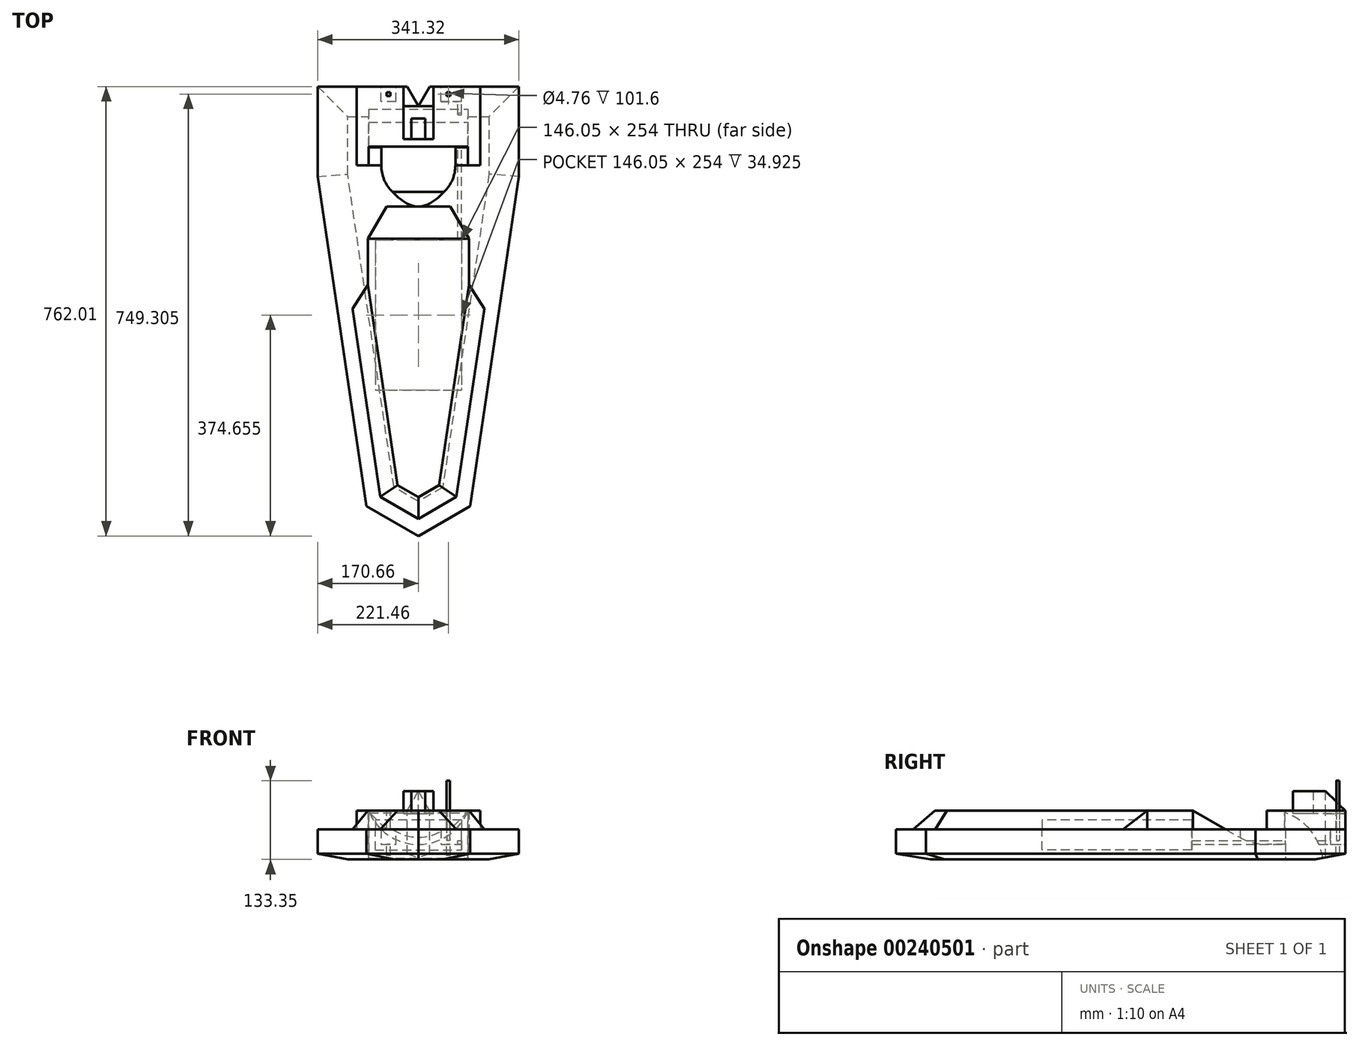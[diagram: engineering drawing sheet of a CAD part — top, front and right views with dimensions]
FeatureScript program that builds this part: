
annotation { "Feature Type Name" : "Feature", "Feature Type Description" : "" }
export const myFeature = defineFeature(function(context is Context, id is Id, definition is map)
    precondition{}
    {
        {
            var Q0;
            Q0=qCreatedBy(makeId("Top.planeOp"),FACE);
            cPlane(context, id + "F0", {"entities" : qUnion([Q0]), "cplaneType" : CPlaneType.OFFSET, "offset" : 65.1 * mm, "oppositeDirection" : true, "width" : 152.4 * mm, "height" : 152.4 * mm});
        }
        {
            var Q0;
            Q0=qCreatedBy(id+"F0.planeOp",FACE);
            var sketch = newSketch(context, id + "F1", { "sketchPlane" : qUnion([Q0])});
            skLineSegment(sketch, "E0", {"start": v(-170.66, -34.93) * mm, "end": v(-87.99, -593.73) * mm});
            skLineSegment(sketch, "E1", {"start": v(-170.66, 117.47) * mm, "end": v(0, 117.48) * mm});
            skLineSegment(sketch, "E2", {"start": v(0, -644.53) * mm, "end": v(-87.99, -593.73) * mm});
            skLineSegment(sketch, "E3", {"start": v(-170.66, -34.93) * mm, "end": v(-170.66, 117.47) * mm});
            skLineSegment(sketch, "E4", {"start": v(-73.03, -142.88) * mm, "end": v(-73.03, -396.88) * mm});
            skLineSegment(sketch, "E5", {"start": v(-73.03, -396.88) * mm, "end": v(0, -396.88) * mm});
            skLineSegment(sketch, "E6", {"start": v(-73.03, -142.88) * mm, "end": v(0, -142.88) * mm});
            skLineSegment(sketch, "E7", {"start": v(0, 117.48) * mm, "end": v(0, -644.53) * mm, "construction": true});
            skLineSegment(sketch, "E8", {"start": v(0, 0) * mm, "end": v(-88.9, 0) * mm, "construction": true});
            skLineSegment(sketch, "E9.MirrorCS", {"start": v(170.66, 117.48) * mm, "end": v(0, 117.48) * mm});
            skLineSegment(sketch, "E10.MirrorCS", {"start": v(170.66, -34.93) * mm, "end": v(170.66, 117.47) * mm});
            skLineSegment(sketch, "E11.MirrorCS", {"start": v(170.66, -34.92) * mm, "end": v(87.99, -593.73) * mm});
            skLineSegment(sketch, "E12.MirrorCS", {"start": v(0, -644.53) * mm, "end": v(87.99, -593.73) * mm});
            skLineSegment(sketch, "E13.MirrorCS", {"start": v(73.03, -396.88) * mm, "end": v(0, -396.88) * mm});
            skLineSegment(sketch, "E14.MirrorCS", {"start": v(73.03, -142.87) * mm, "end": v(73.03, -396.88) * mm});
            skLineSegment(sketch, "E15.MirrorCS", {"start": v(73.03, -142.88) * mm, "end": v(0, -142.88) * mm});
            skLineSegment(sketch, "E16.MirrorCS", {"start": v(0, 0) * mm, "end": v(88.9, 0) * mm, "construction": true});
            skSolve(sketch);
        }
        {
            var Q0;
            Q0=makeQuery(id+"F1.imprint","IMPRINT",FACE,{"disambiguationData":[TD([[makeQuery(id+"F1.imprint","IMPRINT",EDGE,{"derivedFrom":sQuery(id+"F1.wireOp",EDGE,"E4")}),1.0]])]});
            var Q1;
            Q1=makeQuery(id+"F1.imprint","IMPRINT",FACE,{"disambiguationData":[TD([[makeQuery(id+"F1.imprint","IMPRINT",EDGE,{"derivedFrom":sQuery(id+"F1.wireOp",EDGE,"E0")}),1.0]])]});
            extrude(context, id + "F2", {"entities" : qUnion([Q0, Q1]), "oppositeDirection" : true, "depth" : 50.8 * mm});
        }
        {
            var Q0;
            Q0=makeQuery(id+"F1.imprint","IMPRINT",FACE,{"disambiguationData":[TD([[makeQuery(id+"F1.imprint","IMPRINT",EDGE,{"derivedFrom":sQuery(id+"F1.wireOp",EDGE,"E4")}),1.0]])]});
            extrude(context, id + "F3", {"entities" : qUnion([Q0]), "operationType" : NewBodyOperationType.REMOVE, "oppositeDirection" : true, "depth" : 34.92 * mm});
        }
        {
            var Q0;
            Q0=makeQuery(id+"F2.opExtrude","CAP_EDGE",EDGE,{"disambiguationData":[OSD([sQuery(id+"F1.wireOp",EDGE,"E1"),sQuery(id+"F1.wireOp",EDGE,"E9.MirrorCS")])],"isStart":false});
            var Q1;
            Q1=makeQuery(id+"F2.opExtrude","CAP_EDGE",EDGE,{"disambiguationData":[OSD([sQuery(id+"F1.wireOp",EDGE,"E3")])],"isStart":false});
            var Q2;
            Q2=makeQuery(id+"F2.opExtrude","CAP_EDGE",EDGE,{"disambiguationData":[OSD([sQuery(id+"F1.wireOp",EDGE,"E0")])],"isStart":false});
            var Q3;
            Q3=makeQuery(id+"F2.opExtrude","CAP_EDGE",EDGE,{"disambiguationData":[OSD([sQuery(id+"F1.wireOp",EDGE,"E2")])],"isStart":false});
            var Q4;
            Q4=makeQuery(id+"F2.opExtrude","CAP_EDGE",EDGE,{"disambiguationData":[OSD([sQuery(id+"F1.wireOp",EDGE,"E12.MirrorCS")])],"isStart":false});
            var Q5;
            Q5=makeQuery(id+"F2.opExtrude","CAP_EDGE",EDGE,{"disambiguationData":[OSD([sQuery(id+"F1.wireOp",EDGE,"E11.MirrorCS")])],"isStart":false});
            var Q6;
            Q6=makeQuery(id+"F2.opExtrude","CAP_EDGE",EDGE,{"disambiguationData":[OSD([sQuery(id+"F1.wireOp",EDGE,"E10.MirrorCS")])],"isStart":false});
            chamfer(context, id + "F4", {"entities" : qUnion([Q0, Q1, Q2, Q3, Q4, Q5, Q6]), "chamferType" : ChamferType.TWO_OFFSETS, "width1" : 50.8 * mm, "oppositeDirection" : true, "width2" : 9.52 * mm, "tangentPropagation" : true});
        }
        {
            var Q0;
            Q0=qCreatedBy(makeId("Right.planeOp"),FACE);
            var sketch = newSketch(context, id + "F5", { "sketchPlane" : qUnion([Q0])});
            skLineSegment(sketch, "E17", {"start": v(15.88, -65.09) * mm, "end": v(15.88, -115.89) * mm});
            skArc(sketch, "E18", {"start": v(57.15, -65.09) * mm, "mid": v(72.04, -88.84) * mm, "end": v(79.37, -115.89) * mm});
            skLineSegment(sketch, "E19", {"start": v(15.88, -65.09) * mm, "end": v(57.15, -65.09) * mm});
            skLineSegment(sketch, "E20", {"start": v(15.88, -115.89) * mm, "end": v(79.37, -115.89) * mm});
            skSolve(sketch);
        }
        {
            var Q0;
            Q0 = qSketchRegion(id + "F5", true);
            extrude(context, id + "F6", {"entities" : qUnion([Q0]), "operationType" : NewBodyOperationType.REMOVE, "oppositeDirection" : true, "depth" : 168.27 * mm, "symmetric" : true});
        }
        {
            var Q0;
            Q0=qCreatedBy(makeId("Top.planeOp"),FACE);
            cPlane(context, id + "F7", {"entities" : qUnion([Q0]), "cplaneType" : CPlaneType.OFFSET, "offset" : 65.1 * mm, "oppositeDirection" : true, "width" : 152.4 * mm, "height" : 152.4 * mm});
        }
        {
            var Q0;
            Q0=qCreatedBy(id+"F7.planeOp",FACE);
            var sketch = newSketch(context, id + "F8", { "sketchPlane" : qUnion([Q0])});
            skLineSegment(sketch, "E21.0", {"start": v(-170.66, -34.93) * mm, "end": v(-87.99, -593.73) * mm, "construction": true});
            skLineSegment(sketch, "E21.1", {"start": v(0, -644.53) * mm, "end": v(-87.99, -593.73) * mm, "construction": true});
            skLineSegment(sketch, "E21.2", {"start": v(0, -644.53) * mm, "end": v(87.99, -593.73) * mm, "construction": true});
            skLineSegment(sketch, "E21.3", {"start": v(170.66, -34.92) * mm, "end": v(87.99, -593.73) * mm, "construction": true});
            skLineSegment(sketch, "E22", {"start": v(-111.77, -259.4) * mm, "end": v(-64.66, -577.87) * mm});
            skLineSegment(sketch, "E23", {"start": v(-64.66, -577.87) * mm, "end": v(0, -615.2) * mm});
            skLineSegment(sketch, "E24", {"start": v(0, -615.2) * mm, "end": v(64.66, -577.87) * mm});
            skLineSegment(sketch, "E25", {"start": v(64.66, -577.87) * mm, "end": v(111.77, -259.4) * mm});
            skLineSegment(sketch, "E26.0", {"start": v(-73.03, -396.88) * mm, "end": v(73.03, -396.87) * mm});
            skLineSegment(sketch, "E26.1", {"start": v(73.03, -142.87) * mm, "end": v(-73.03, -142.88) * mm});
            skLineSegment(sketch, "E26.2", {"start": v(73.03, -142.87) * mm, "end": v(73.03, -396.87) * mm});
            skLineSegment(sketch, "E26.3", {"start": v(-73.03, -142.88) * mm, "end": v(-73.03, -396.88) * mm});
            skLineSegment(sketch, "E27", {"start": v(-53.97, -85.73) * mm, "end": v(53.98, -85.72) * mm});
            skLineSegment(sketch, "E28", {"start": v(0, -615.2) * mm, "end": v(0, -52.66) * mm, "construction": true});
            skLineSegment(sketch, "E29", {"start": v(85.73, -140.72) * mm, "end": v(85.73, -218.5) * mm});
            skLineSegment(sketch, "E30", {"start": v(-85.72, -140.72) * mm, "end": v(-85.72, -218.5) * mm});
            skLineSegment(sketch, "E31", {"start": v(85.73, -218.5) * mm, "end": v(111.77, -259.4) * mm});
            skLineSegment(sketch, "E32", {"start": v(-85.72, -218.5) * mm, "end": v(-111.77, -259.4) * mm});
            skLineSegment(sketch, "E33", {"start": v(-111.77, -259.4) * mm, "end": v(111.77, -259.4) * mm, "construction": true});
            skLineSegment(sketch, "E34", {"start": v(-85.72, -140.72) * mm, "end": v(-53.97, -85.72) * mm});
            skLineSegment(sketch, "E35", {"start": v(85.73, -140.72) * mm, "end": v(53.98, -85.72) * mm});
            skLineSegment(sketch, "E36", {"start": v(-85.72, -140.72) * mm, "end": v(85.73, -140.72) * mm, "construction": true});
            skSolve(sketch);
        }
        {
            var Q0;
            Q0 = qSketchRegion(id + "F8", true);
            var Q1;
            Q1=makeQuery(id+"F8.imprint","IMPRINT",FACE,{"disambiguationData":[TD([[makeQuery(id+"F8.imprint","IMPRINT",EDGE,{"derivedFrom":sQuery(id+"F8.wireOp",EDGE,"E26.0")}),1.0]])]});
            extrude(context, id + "F9", {"entities" : qUnion([Q0, Q1]), "depth" : 31.75 * mm});
        }
        {
            var Q0;
            Q0=makeQuery(id+"F9.opExtrude","CAP_EDGE",EDGE,{"disambiguationData":[OSD([sQuery(id+"F8.wireOp",EDGE,"E25")])],"isStart":false});
            var Q1;
            Q1=makeQuery(id+"F9.opExtrude","CAP_EDGE",EDGE,{"disambiguationData":[OSD([sQuery(id+"F8.wireOp",EDGE,"E24")])],"isStart":false});
            var Q2;
            Q2=makeQuery(id+"F9.opExtrude","CAP_EDGE",EDGE,{"disambiguationData":[OSD([sQuery(id+"F8.wireOp",EDGE,"E23")])],"isStart":false});
            var Q3;
            Q3=makeQuery(id+"F9.opExtrude","CAP_EDGE",EDGE,{"disambiguationData":[OSD([sQuery(id+"F8.wireOp",EDGE,"E22")])],"isStart":false});
            chamfer(context, id + "F10", {"entities" : qUnion([Q0, Q1, Q2, Q3]), "width" : 31.75 * mm, "tangentPropagation" : true});
        }
        {
            var Q0;
            Q0=makeQuery(id+"F9.opExtrude","CAP_EDGE",EDGE,{"disambiguationData":[OSD([sQuery(id+"F8.wireOp",EDGE,"E27")])],"isStart":false});
            chamfer(context, id + "F11", {"entities" : qUnion([Q0]), "chamferType" : ChamferType.OFFSET_ANGLE, "width" : 31.75 * mm, "oppositeDirection" : false, "angle" : 60 * degree, "tangentPropagation" : true});
        }
        {
            var Q0;
            Q0=makeQuery(id+"F8.imprint","IMPRINT",FACE,{"disambiguationData":[TD([[makeQuery(id+"F8.imprint","IMPRINT",EDGE,{"derivedFrom":sQuery(id+"F8.wireOp",EDGE,"E26.0")}),1.0]])]});
            extrude(context, id + "F12", {"entities" : qUnion([Q0]), "operationType" : NewBodyOperationType.REMOVE, "depth" : 15.88 * mm});
        }
        {
            var Q0;
            Q0=qCreatedBy(id+"F7.planeOp",FACE);
            var sketch = newSketch(context, id + "F13", { "sketchPlane" : qUnion([Q0])});
            skLineSegment(sketch, "E37.bottom", {"start": v(-104.78, 117.48) * mm, "end": v(104.78, 117.48) * mm});
            skLineSegment(sketch, "E37.top", {"start": v(-104.77, -15.88) * mm, "end": v(104.78, -15.88) * mm});
            skLineSegment(sketch, "E37.left", {"start": v(-104.78, 117.48) * mm, "end": v(-104.77, -15.88) * mm});
            skLineSegment(sketch, "E37.right", {"start": v(104.78, 117.48) * mm, "end": v(104.78, -15.87) * mm});
            skLineSegment(sketch, "E38", {"start": v(0, 117.48) * mm, "end": v(0, -15.88) * mm, "construction": true});
            skSolve(sketch);
        }
        {
            var Q0;
            Q0 = qSketchRegion(id + "F13", true);
            extrude(context, id + "F14", {"entities" : qUnion([Q0]), "depth" : 31.75 * mm});
        }
        {
            var Q0;
            Q0=makeQuery(id+"F14.opExtrude","SWEPT_FACE",FACE,{"disambiguationData":[OSD([sQuery(id+"F13.wireOp",EDGE,"E37.top")])]});
            cPlane(context, id + "F15", {"entities" : qUnion([Q0]), "cplaneType" : CPlaneType.OFFSET, "offset" : 15.88 * mm, "oppositeDirection" : true, "width" : 152.4 * mm, "height" : 152.4 * mm});
        }
        {
            var Q0;
            Q0=qCreatedBy(id+"F15.planeOp",FACE);
            var sketch = newSketch(context, id + "F16", { "sketchPlane" : qUnion([Q0])});
            skCircle(sketch, "E39", {"center": v(0, 0) * mm, "radius": 90.49 * mm});
            skSolve(sketch);
        }
        {
            var Q0;
            Q0=qCreatedBy(makeId("Right.planeOp"),FACE);
            var sketch = newSketch(context, id + "F17", { "sketchPlane" : qUnion([Q0])});
            skArc(sketch, "E40.0", {"start": v(57.15, -65.09) * mm, "mid": v(72.04, -88.84) * mm, "end": v(79.37, -115.89) * mm, "construction": true});
            skArc(sketch, "E41", {"start": v(57.15, -65.09) * mm, "mid": v(37.8, -47.87) * mm, "end": v(14.5, -36.51) * mm});
            skLineSegment(sketch, "E42", {"start": v(14.5, -36.51) * mm, "end": v(14.5, -33.34) * mm, "construction": true});
            skLineSegment(sketch, "E43", {"start": v(79.37, -115.89) * mm, "end": v(-15.23, -115.89) * mm, "construction": true});
            skLineSegment(sketch, "E44", {"start": v(57.15, -65.09) * mm, "end": v(-15.23, -65.09) * mm, "construction": true});
            skLineSegment(sketch, "E45", {"start": v(14.5, -33.34) * mm, "end": v(-34.43, -33.34) * mm, "construction": true});
            skLineSegment(sketch, "E46", {"start": v(14.5, -36.51) * mm, "end": v(14.5, -65.09) * mm});
            skLineSegment(sketch, "E47", {"start": v(14.5, -65.09) * mm, "end": v(57.15, -65.09) * mm});
            skSolve(sketch);
        }
        {
            var Q0;
            Q0=makeQuery(id+"F17.imprint","IMPRINT",FACE,{"disambiguationData":[TD([[makeQuery(id+"F17.imprint","IMPRINT",EDGE,{"derivedFrom":sQuery(id+"F17.wireOp",EDGE,"E41")}),1.0]])]});
            extrude(context, id + "F18", {"entities" : qUnion([Q0]), "operationType" : NewBodyOperationType.REMOVE, "oppositeDirection" : true, "depth" : 168.27 * mm, "symmetric" : true});
        }
        {
            var Q0;
            Q0 = qSketchRegion(id + "F16", true);
            var Q1;
            Q1=makeQuery(id+"F6.boolean.opBoolean","COPY",FACE,{"derivedFrom":makeQuery(id+"F6.opExtrude","SWEPT_FACE",FACE,{"disambiguationData":[OSD([sQuery(id+"F5.wireOp",EDGE,"E17")])]})});
            var Q2;
            Q2=makeQuery(id+"F14.opExtrude","SWEPT_FACE",FACE,{"disambiguationData":[OSD([sQuery(id+"F13.wireOp",EDGE,"E37.top")])]});
            extrude(context, id + "F19", {"entities" : qUnion([Q0]), "operationType" : NewBodyOperationType.REMOVE, "endBound" : BoundingType.UP_TO_SURFACE, "oppositeDirection" : true, "endBoundEntityFace" : qUnion([Q1]), "depth" : 30.16 * mm, "hasSecondDirection" : true, "secondDirectionBound" : BoundingType.UP_TO_SURFACE, "secondDirectionOppositeDirection" : false, "secondDirectionBoundEntityFace" : qUnion([Q2]), "secondDirectionDepth" : 25.4 * mm});
        }
        {
            var Q0;
            Q0=qCreatedBy(makeId("Right.planeOp"),FACE);
            var sketch = newSketch(context, id + "F20", { "sketchPlane" : qUnion([Q0])});
            skLineSegment(sketch, "E48", {"start": v(0, -90.49) * mm, "end": v(-85.73, -65.09) * mm, "construction": true});
            skPoint(sketch, "E49.0", {"position": v(0, 0) * mm});
            skArc(sketch, "E50", {"start": v(-15.87, -90.49) * mm, "mid": v(-39.3, -87.4) * mm, "end": v(-61.12, -78.36) * mm});
            skLineSegment(sketch, "E51", {"start": v(-15.87, 0) * mm, "end": v(-61.12, -78.36) * mm, "construction": true});
            skLineSegment(sketch, "E52", {"start": v(-61.12, -78.36) * mm, "end": v(-85.73, -65.09) * mm});
            skLineSegment(sketch, "E53", {"start": v(-85.73, -65.09) * mm, "end": v(0, -65.09) * mm});
            skLineSegment(sketch, "E54", {"start": v(0, -65.09) * mm, "end": v(0, -90.49) * mm});
            skLineSegment(sketch, "E55", {"start": v(0, 0) * mm, "end": v(-85.73, 0) * mm, "construction": true});
            skLineSegment(sketch, "E56", {"start": v(0, -90.49) * mm, "end": v(-15.87, -90.49) * mm});
            skSolve(sketch);
        }
        {
            var Q0;
            Q0 = qSketchRegion(id + "F20", true);
            var Q1;
            Q1=sQuery(id+"F20.wireOp",EDGE,"E55");
            revolve(context, id + "F21", {"operationType" : NewBodyOperationType.REMOVE, "entities" : qUnion([Q0]), "axis" : qUnion([Q1]), "revolveType" : RevolveType.FULL, "oppositeDirection" : true});
        }
        {
            var Q0;
            Q0=makeQuery(id+"F4.opChamfer","BLEND_FACE",FACE,{"disambiguationData":[OSD([sQuery(id+"F1.wireOp",EDGE,"E1"),sQuery(id+"F1.wireOp",EDGE,"E9.MirrorCS")])]});
            var Q1;
            Q1=makeQuery(id+"F6.boolean.opBoolean","INTERSECT",EDGE,{"derivedFrom":[makeQuery(id+"F4.opChamfer","BLEND_FACE",FACE,{"disambiguationData":[OSD([sQuery(id+"F1.wireOp",EDGE,"E1"),sQuery(id+"F1.wireOp",EDGE,"E9.MirrorCS")])]}),makeQuery(id+"F6.opExtrude","SWEPT_FACE",FACE,{"disambiguationData":[OSD([sQuery(id+"F5.wireOp",EDGE,"E18")])]})]});
            cPlane(context, id + "F22", {"entities" : qUnion([Q0, Q1]), "cplaneType" : CPlaneType.LINE_ANGLE, "offset" : 25.4 * mm, "angle" : 90 * degree, "width" : 152.4 * mm, "height" : 152.4 * mm});
        }
        {
            var Q0;
            Q0=makeQuery(id+"F14.opExtrude","CAP_FACE",FACE,{"disambiguationData":[OSD([sQuery(id+"F13.wireOp",EDGE,"E37.bottom"),sQuery(id+"F13.wireOp",EDGE,"E37.top"),sQuery(id+"F13.wireOp",EDGE,"E37.left"),sQuery(id+"F13.wireOp",EDGE,"E37.right")])],"isStart":false});
            var sketch = newSketch(context, id + "F23", { "sketchPlane" : qUnion([Q0])});
            skLineSegment(sketch, "E57", {"start": v(0, 117.47) * mm, "end": v(0, 15.88) * mm, "construction": true});
            skLineSegment(sketch, "E58", {"start": v(-25.4, 117.47) * mm, "end": v(-25.4, 28.58) * mm});
            skLineSegment(sketch, "E59", {"start": v(-25.4, 28.58) * mm, "end": v(25.4, 28.58) * mm});
            skLineSegment(sketch, "E60", {"start": v(25.4, 28.57) * mm, "end": v(25.4, 117.48) * mm});
            skLineSegment(sketch, "E61", {"start": v(-25.4, 117.48) * mm, "end": v(25.4, 117.48) * mm});
            skSolve(sketch);
        }
        {
            var Q0;
            Q0 = qSketchRegion(id + "F23", true);
            extrude(context, id + "F24", {"entities" : qUnion([Q0]), "operationType" : NewBodyOperationType.REMOVE, "oppositeDirection" : true, "depth" : 4.76 * mm});
        }
        {
            var Q0;
            Q0=qCreatedBy(makeId("Top.planeOp"),FACE);
            cPlane(context, id + "F25", {"entities" : qUnion([Q0]), "cplaneType" : CPlaneType.OFFSET, "offset" : 38.1 * mm, "oppositeDirection" : true, "width" : 152.4 * mm, "height" : 152.4 * mm});
        }
        {
            var Q0;
            Q0=qCreatedBy(id+"F25.planeOp",FACE);
            var sketch = newSketch(context, id + "F26", { "sketchPlane" : qUnion([Q0])});
            skLineSegment(sketch, "E62", {"start": v(0, 24.05) * mm, "end": v(0, -116.01) * mm, "construction": true});
            skPoint(sketch, "E62.startSnap0", {"position": v(0, 117.48) * mm});
            skLineSegment(sketch, "E63", {"start": v(-25.4, 117.48) * mm, "end": v(25.4, 117.48) * mm});
            skLineSegment(sketch, "E64", {"start": v(25.4, 117.48) * mm, "end": v(25.4, 28.58) * mm});
            skLineSegment(sketch, "E65", {"start": v(25.4, 28.58) * mm, "end": v(-25.4, 28.58) * mm});
            skLineSegment(sketch, "E66", {"start": v(-25.4, 28.58) * mm, "end": v(-25.4, 117.48) * mm});
            skSolve(sketch);
        }
        {
            var Q0;
            Q0 = qSketchRegion(id + "F26", true);
            extrude(context, id + "F27", {"entities" : qUnion([Q0]), "depth" : 38.1 * mm});
        }
        {
            var Q0;
            Q0=makeQuery(id+"F27.opExtrude","CAP_FACE",FACE,{"disambiguationData":[OSD([sQuery(id+"F26.wireOp",EDGE,"E63"),sQuery(id+"F26.wireOp",EDGE,"E64"),sQuery(id+"F26.wireOp",EDGE,"E65"),sQuery(id+"F26.wireOp",EDGE,"E66")])],"isStart":false});
            var sketch = newSketch(context, id + "F28", { "sketchPlane" : qUnion([Q0])});
            skLineSegment(sketch, "E67", {"start": v(0, 11.6) * mm, "end": v(0, -95.3) * mm, "construction": true});
            skPoint(sketch, "E67.startSnap0", {"position": v(0, 117.48) * mm});
            skLineSegment(sketch, "E68", {"start": v(11.9, 28.58) * mm, "end": v(11.9, 63.5) * mm});
            skLineSegment(sketch, "E69", {"start": v(11.9, 63.5) * mm, "end": v(-11.9, 63.5) * mm});
            skLineSegment(sketch, "E70", {"start": v(-11.9, 63.5) * mm, "end": v(-11.9, 28.58) * mm});
            skLineSegment(sketch, "E71", {"start": v(-11.9, 28.57) * mm, "end": v(11.9, 28.58) * mm});
            skSolve(sketch);
        }
        {
            var Q0;
            Q0 = qSketchRegion(id + "F28", true);
            extrude(context, id + "F29", {"entities" : qUnion([Q0]), "operationType" : NewBodyOperationType.REMOVE, "endBound" : BoundingType.UP_TO_NEXT, "oppositeDirection" : true, "depth" : 25.4 * mm});
        }
        {
            var Q0;
            Q0=makeQuery(id+"F27.opExtrude","CAP_EDGE",EDGE,{"disambiguationData":[OSD([sQuery(id+"F26.wireOp",EDGE,"E63")])],"isStart":false});
            chamfer(context, id + "F30", {"entities" : qUnion([Q0]), "width" : 33.34 * mm, "tangentPropagation" : true});
        }
        {
            var Q0;
            Q0=makeQuery(id+"F27.opExtrude","CAP_FACE",FACE,{"disambiguationData":[OSD([sQuery(id+"F26.wireOp",EDGE,"E63"),sQuery(id+"F26.wireOp",EDGE,"E64"),sQuery(id+"F26.wireOp",EDGE,"E65"),sQuery(id+"F26.wireOp",EDGE,"E66")])],"isStart":false});
            var sketch = newSketch(context, id + "F31", { "sketchPlane" : qUnion([Q0])});
            skLineSegment(sketch, "E72", {"start": v(0, 3.76) * mm, "end": v(0, 84.14) * mm, "construction": true});
            skLineSegment(sketch, "E73", {"start": v(0, 84.14) * mm, "end": v(19.05, 117.48) * mm});
            skLineSegment(sketch, "E74", {"start": v(0, 84.14) * mm, "end": v(-19.05, 117.48) * mm});
            skLineSegment(sketch, "E75", {"start": v(-19.05, 117.48) * mm, "end": v(19.05, 117.48) * mm});
            skSolve(sketch);
        }
        {
            var Q0;
            Q0 = qSketchRegion(id + "F31", true);
            extrude(context, id + "F32", {"entities" : qUnion([Q0]), "operationType" : NewBodyOperationType.REMOVE, "endBound" : BoundingType.THROUGH_ALL, "oppositeDirection" : true, "depth" : 25.4 * mm});
        }
        {
            var Q0;
            Q0=makeQuery(id+"F14.opExtrude","CAP_FACE",FACE,{"disambiguationData":[OSD([sQuery(id+"F13.wireOp",EDGE,"E37.bottom"),sQuery(id+"F13.wireOp",EDGE,"E37.top"),sQuery(id+"F13.wireOp",EDGE,"E37.left"),sQuery(id+"F13.wireOp",EDGE,"E37.right")])],"isStart":false});
            var sketch = newSketch(context, id + "F33", { "sketchPlane" : qUnion([Q0])});
            skLineSegment(sketch, "E76.bottom", {"start": v(-53.97, 107.95) * mm, "end": v(-47.63, 107.95) * mm});
            skLineSegment(sketch, "E76.top", {"start": v(-53.97, 101.6) * mm, "end": v(-47.63, 101.6) * mm});
            skLineSegment(sketch, "E76.left", {"start": v(-53.98, 107.95) * mm, "end": v(-53.98, 101.6) * mm});
            skLineSegment(sketch, "E76.right", {"start": v(-47.63, 107.95) * mm, "end": v(-47.63, 101.6) * mm});
            skLineSegment(sketch, "E77.bottom", {"start": v(47.63, 107.95) * mm, "end": v(53.98, 107.95) * mm});
            skLineSegment(sketch, "E77.top", {"start": v(47.63, 101.6) * mm, "end": v(53.98, 101.6) * mm});
            skLineSegment(sketch, "E77.left", {"start": v(47.63, 107.95) * mm, "end": v(47.63, 101.6) * mm});
            skLineSegment(sketch, "E77.right", {"start": v(53.98, 107.95) * mm, "end": v(53.98, 101.6) * mm});
            skLineSegment(sketch, "E78", {"start": v(-50.8, 107.95) * mm, "end": v(-50.8, 101.6) * mm, "construction": true});
            skLineSegment(sketch, "E79", {"start": v(50.8, 107.95) * mm, "end": v(50.8, 101.6) * mm, "construction": true});
            skLineSegment(sketch, "E80", {"start": v(0, 15.88) * mm, "end": v(0, 25.14) * mm, "construction": true});
            skSolve(sketch);
        }
        {
            var Q0;
            Q0 = qSketchRegion(id + "F33", true);
            extrude(context, id + "F34", {"entities" : qUnion([Q0]), "operationType" : NewBodyOperationType.REMOVE, "endBound" : BoundingType.THROUGH_ALL, "oppositeDirection" : true, "depth" : 25.4 * mm});
        }
        {
            var Q0;
            Q0=makeQuery(id+"F2.opExtrude","SWEPT_FACE",FACE,{"disambiguationData":[OSD([sQuery(id+"F1.wireOp",EDGE,"E1"),sQuery(id+"F1.wireOp",EDGE,"E9.MirrorCS")])]});
            var sketch = newSketch(context, id + "F35", { "sketchPlane" : qUnion([Q0])});
            skLineSegment(sketch, "E81", {"start": v(0, 0) * mm, "end": v(0, -106.36) * mm, "construction": true});
            skLineSegment(sketch, "E82", {"start": v(-73.02, -65.09) * mm, "end": v(-38.1, -65.09) * mm});
            skLineSegment(sketch, "E83", {"start": v(-38.1, -65.09) * mm, "end": v(-38.1, -90.49) * mm});
            skLineSegment(sketch, "E84", {"start": v(-38.1, -90.49) * mm, "end": v(-73.02, -90.49) * mm});
            skLineSegment(sketch, "E85", {"start": v(-73.03, -90.49) * mm, "end": v(-73.03, -65.09) * mm});
            skLineSegment(sketch, "E86", {"start": v(38.1, -65.09) * mm, "end": v(63.5, -65.09) * mm});
            skLineSegment(sketch, "E87", {"start": v(63.5, -65.09) * mm, "end": v(63.5, -90.49) * mm});
            skLineSegment(sketch, "E88", {"start": v(63.5, -90.49) * mm, "end": v(38.1, -90.49) * mm});
            skLineSegment(sketch, "E89", {"start": v(38.1, -90.49) * mm, "end": v(38.1, -65.09) * mm});
            skSolve(sketch);
        }
        {
            var Q0;
            Q0 = qSketchRegion(id + "F35", true);
            extrude(context, id + "F36", {"entities" : qUnion([Q0]), "operationType" : NewBodyOperationType.REMOVE, "oppositeDirection" : true, "depth" : 25.4 * mm});
        }
        {
            var Q0;
            Q0=makeQuery(id+"F36.boolean.opBoolean","COPY",FACE,{"derivedFrom":makeQuery(id+"F36.opExtrude","CAP_FACE",FACE,{"disambiguationData":[OSD([sQuery(id+"F35.wireOp",EDGE,"E82"),sQuery(id+"F35.wireOp",EDGE,"E83"),sQuery(id+"F35.wireOp",EDGE,"E84"),sQuery(id+"F35.wireOp",EDGE,"E85")])],"isStart":false})});
            var sketch = newSketch(context, id + "F37", { "sketchPlane" : qUnion([Q0])});
            skLineSegment(sketch, "E90", {"start": v(-73.03, -84.14) * mm, "end": v(-66.67, -84.14) * mm});
            skLineSegment(sketch, "E91", {"start": v(-66.67, -84.14) * mm, "end": v(-66.67, -90.49) * mm});
            skLineSegment(sketch, "E92", {"start": v(-66.67, -90.49) * mm, "end": v(-73.03, -90.49) * mm});
            skLineSegment(sketch, "E93", {"start": v(-73.03, -90.49) * mm, "end": v(-73.03, -84.14) * mm});
            skSolve(sketch);
        }
        {
            var Q0;
            Q0 = qSketchRegion(id + "F37", true);
            var Q1;
            Q1=makeQuery(id+"F3.boolean.opBoolean","COPY",FACE,{"derivedFrom":makeQuery(id+"F3.opExtrude","SWEPT_FACE",FACE,{"disambiguationData":[OSD([sQuery(id+"F1.wireOp",EDGE,"E6"),sQuery(id+"F1.wireOp",EDGE,"E15.MirrorCS")])]})});
            extrude(context, id + "F38", {"entities" : qUnion([Q0]), "operationType" : NewBodyOperationType.REMOVE, "endBound" : BoundingType.UP_TO_SURFACE, "oppositeDirection" : true, "endBoundEntityFace" : qUnion([Q1]), "depth" : 25.4 * mm});
        }
        {
            var Q0;
            Q0 = qSketchRegion(id + "F13", true);
            var sketch = newSketch(context, id + "F39", { "sketchPlane" : qUnion([Q0])});
            skLineSegment(sketch, "E94.bottom", {"start": v(47.62, 107.95) * mm, "end": v(53.97, 107.95) * mm});
            skLineSegment(sketch, "E94.top", {"start": v(47.62, 101.6) * mm, "end": v(53.97, 101.6) * mm});
            skLineSegment(sketch, "E94.left", {"start": v(47.62, 107.95) * mm, "end": v(47.62, 101.6) * mm});
            skLineSegment(sketch, "E94.right", {"start": v(53.97, 107.95) * mm, "end": v(53.97, 101.6) * mm});
            skLineSegment(sketch, "E95", {"start": v(50.8, 107.95) * mm, "end": v(50.8, 101.6) * mm, "construction": true});
            skLineSegment(sketch, "E96", {"start": v(48.02, 107.55) * mm, "end": v(48.02, 102) * mm});
            skLineSegment(sketch, "E97", {"start": v(48.02, 102) * mm, "end": v(53.58, 102) * mm});
            skLineSegment(sketch, "E98", {"start": v(53.58, 102) * mm, "end": v(53.58, 107.55) * mm});
            skLineSegment(sketch, "E99", {"start": v(53.58, 107.55) * mm, "end": v(48.02, 107.55) * mm});
            skLineSegment(sketch, "E100", {"start": v(48.02, 104.77) * mm, "end": v(53.58, 104.77) * mm, "construction": true});
            skSolve(sketch);
        }
        {
            var Q0;
            Q0 = qSketchRegion(id + "F39", true);
            extrude(context, id + "F40", {"entities" : qUnion([Q0]), "depth" : 31.75 * mm});
        }
        {
            var Q0;
            Q0=qCreatedBy(id+"F7.planeOp",FACE);
            var sketch = newSketch(context, id + "F41", { "sketchPlane" : qUnion([Q0])});
            skCircle(sketch, "E101", {"center": v(50.8, 104.78) * mm, "radius": 2.78 * mm});
            skCircle(sketch, "E102", {"center": v(50.8, 104.78) * mm, "radius": 2.38 * mm});
            skSolve(sketch);
        }
        {
            var Q0;
            Q0 = qSketchRegion(id + "F41", true);
            extrude(context, id + "F42", {"entities" : qUnion([Q0]), "depth" : 82.55 * mm, "hasSecondDirection" : true, "secondDirectionOppositeDirection" : true, "secondDirectionDepth" : 19.05 * mm});
        }
    });
